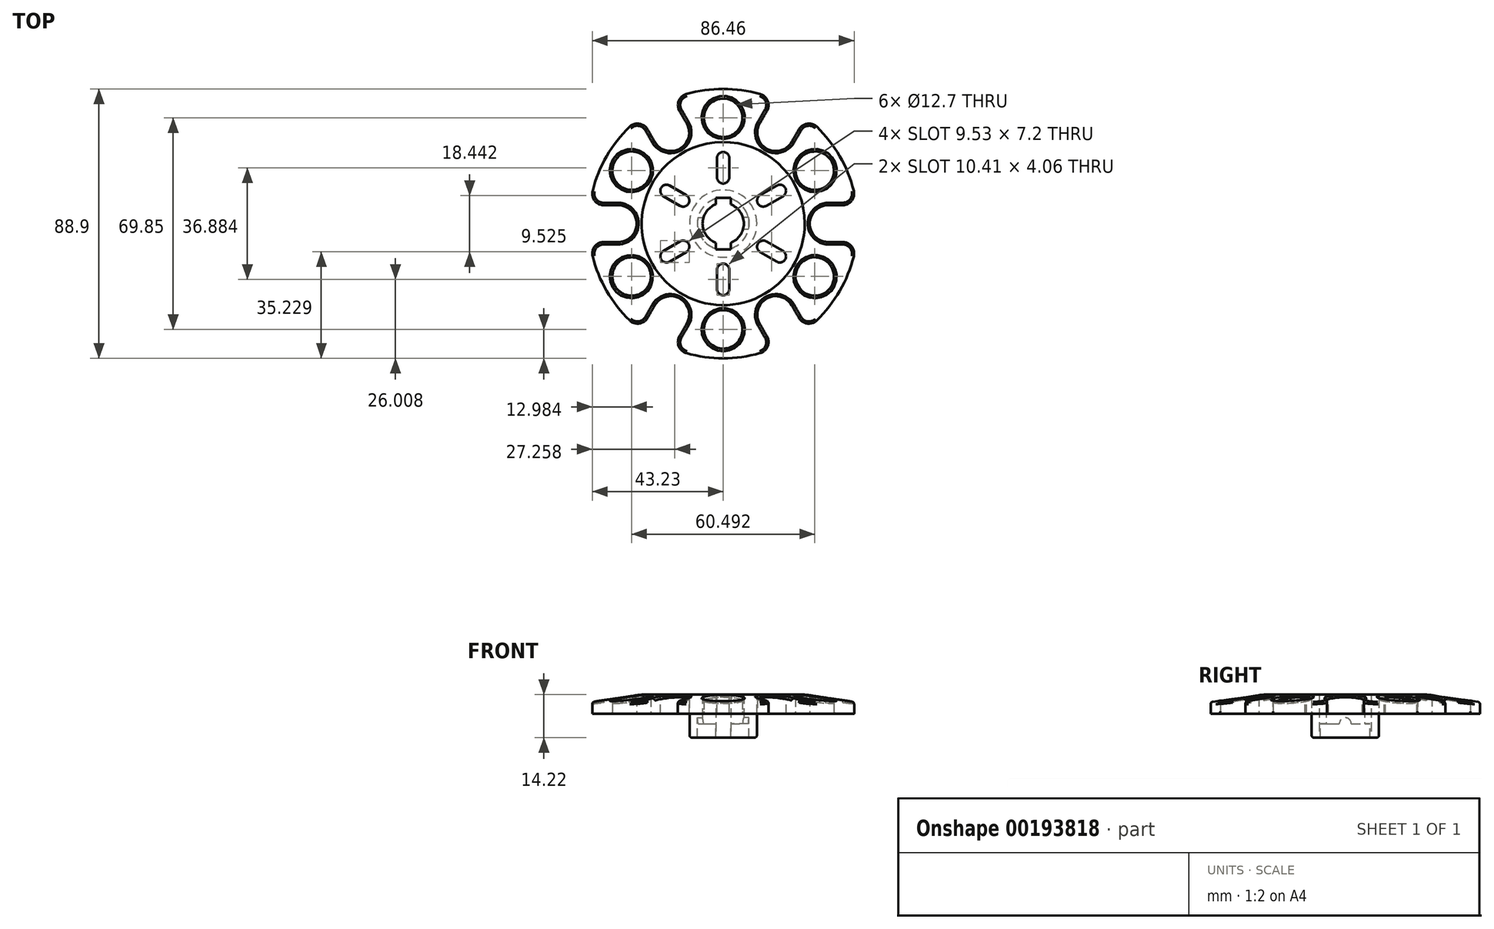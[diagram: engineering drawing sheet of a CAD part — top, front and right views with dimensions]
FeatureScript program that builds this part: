
annotation { "Feature Type Name" : "Feature", "Feature Type Description" : "" }
export const myFeature = defineFeature(function(context is Context, id is Id, definition is map)
    precondition{}
    {
        {
            var Q0;
            Q0=qCreatedBy(makeId("Top.planeOp"),FACE);
            var sketch = newSketch(context, id + "F0", { "sketchPlane" : qUnion([Q0])});
            skCircle(sketch, "E0", {"center": v(0, 0) * mm, "radius": 44.45 * mm, "construction": true});
            skArc(sketch, "E1", {"start": v(-2.48, 6.35) * mm, "mid": v(-6.82, 0) * mm, "end": v(-2.48, -6.35) * mm});
            skCircle(sketch, "E2", {"center": v(0, 0) * mm, "radius": 8.55 * mm, "construction": true});
            skLineSegment(sketch, "E3", {"start": v(0, 0) * mm, "end": v(0, 49.33) * mm, "construction": true});
            skLineSegment(sketch, "E4", {"start": v(-14.44, 42.04) * mm, "end": v(-14.44, 0) * mm, "construction": true});
            skArc(sketch, "E5", {"start": v(0, 44.45) * mm, "mid": v(-6.16, 44.02) * mm, "end": v(-12.2, 42.74) * mm});
            skLineSegment(sketch, "E6", {"start": v(0, 0) * mm, "end": v(-4.27, 7.4) * mm, "construction": true});
            skLineSegment(sketch, "E7", {"start": v(-14.44, 37.2) * mm, "end": v(-12.06, 33.07) * mm});
            skArc(sketch, "E8", {"start": v(-14.44, 37.2) * mm, "mid": v(-14.67, 40.52) * mm, "end": v(-12.2, 42.74) * mm});
            skCircle(sketch, "E9", {"center": v(0, 0) * mm, "radius": 28.58 * mm, "construction": true});
            skLineSegment(sketch, "E10.trimOffspring", {"start": v(-14.29, 24.75) * mm, "end": v(-22.23, 38.5) * mm, "construction": true});
            skArc(sketch, "E11", {"start": v(-14.44, 24.66) * mm, "mid": v(-11.47, 28.36) * mm, "end": v(-12.06, 33.07) * mm});
            skPoint(sketch, "E11.second.point", {"position": v(-20.38, 35.3) * mm});
            skPoint(sketch, "E11.third.point", {"position": v(-12.06, 33.07) * mm});
            skArc(sketch, "E12.MirrorCS", {"start": v(0, 44.45) * mm, "mid": v(6.16, 44.02) * mm, "end": v(12.2, 42.74) * mm});
            skArc(sketch, "E13.MirrorCS", {"start": v(14.44, 37.2) * mm, "mid": v(14.67, 40.52) * mm, "end": v(12.2, 42.74) * mm});
            skLineSegment(sketch, "E14.MirrorCS", {"start": v(14.44, 37.2) * mm, "end": v(12.06, 33.07) * mm});
            skArc(sketch, "E15.MirrorCS", {"start": v(14.44, 24.66) * mm, "mid": v(11.47, 28.36) * mm, "end": v(12.06, 33.07) * mm});
            skCircle(sketch, "E16", {"center": v(0, 34.93) * mm, "radius": 6.35 * mm});
            skLineSegment(sketch, "E17.anchor1", {"start": v(0, 0) * mm, "end": v(-14.44, 24.66) * mm, "construction": true});
            skLineSegment(sketch, "E17.anchor2", {"start": v(0, 0) * mm, "end": v(-14.44, 24.66) * mm, "construction": true});
            skArc(sketch, "E18.1.0", {"start": v(-28.58, -0.17) * mm, "mid": v(-30.3, 4.25) * mm, "end": v(-34.67, 6.1) * mm});
            skLineSegment(sketch, "E18.1.1", {"start": v(-39.44, 6.1) * mm, "end": v(-34.67, 6.1) * mm});
            skArc(sketch, "E18.1.2", {"start": v(-39.44, 6.1) * mm, "mid": v(-42.43, 7.56) * mm, "end": v(-43.12, 10.8) * mm});
            skCircle(sketch, "E18.1.3", {"center": v(-30.25, 17.46) * mm, "radius": 6.35 * mm});
            skArc(sketch, "E18.1.4", {"start": v(-25, 31.1) * mm, "mid": v(-27.76, 32.97) * mm, "end": v(-30.92, 31.93) * mm});
            skLineSegment(sketch, "E18.1.5", {"start": v(-25, 31.1) * mm, "end": v(-22.61, 26.98) * mm});
            skArc(sketch, "E18.1.6", {"start": v(-14.14, 24.84) * mm, "mid": v(-18.83, 24.12) * mm, "end": v(-22.61, 26.98) * mm});
            skArc(sketch, "E18.1.7", {"start": v(-38.5, 22.22) * mm, "mid": v(-35.04, 27.34) * mm, "end": v(-30.92, 31.93) * mm});
            skArc(sketch, "E18.1.8", {"start": v(-38.5, 22.23) * mm, "mid": v(-35.04, 27.34) * mm, "end": v(-30.92, 31.93) * mm});
            skArc(sketch, "E18.1.9", {"start": v(-38.5, 22.23) * mm, "mid": v(-35.04, 27.34) * mm, "end": v(-30.92, 31.93) * mm});
            skArc(sketch, "E18.1.10", {"start": v(-38.5, 22.23) * mm, "mid": v(-35.04, 27.34) * mm, "end": v(-30.92, 31.93) * mm});
            skArc(sketch, "E18.1.11", {"start": v(-38.5, 22.23) * mm, "mid": v(-35.04, 27.34) * mm, "end": v(-30.92, 31.93) * mm});
            skArc(sketch, "E18.1.12", {"start": v(-38.5, 22.23) * mm, "mid": v(-35.04, 27.34) * mm, "end": v(-30.92, 31.93) * mm});
            skArc(sketch, "E18.1.13", {"start": v(-38.5, 22.23) * mm, "mid": v(-41.2, 16.68) * mm, "end": v(-43.12, 10.8) * mm});
            skArc(sketch, "E18.1.14", {"start": v(-38.5, 22.23) * mm, "mid": v(-41.2, 16.68) * mm, "end": v(-43.12, 10.8) * mm});
            skArc(sketch, "E18.1.15", {"start": v(-38.5, 22.22) * mm, "mid": v(-41.2, 16.68) * mm, "end": v(-43.12, 10.8) * mm});
            skArc(sketch, "E18.1.16", {"start": v(-38.5, 22.23) * mm, "mid": v(-41.2, 16.68) * mm, "end": v(-43.12, 10.8) * mm});
            skArc(sketch, "E18.1.17", {"start": v(-38.5, 22.23) * mm, "mid": v(-41.2, 16.68) * mm, "end": v(-43.12, 10.8) * mm});
            skArc(sketch, "E18.1.18", {"start": v(-38.5, 22.23) * mm, "mid": v(-41.2, 16.68) * mm, "end": v(-43.12, 10.8) * mm});
            skArc(sketch, "E18.2.0", {"start": v(-14.14, -24.84) * mm, "mid": v(-18.83, -24.12) * mm, "end": v(-22.61, -26.98) * mm});
            skLineSegment(sketch, "E18.2.1", {"start": v(-25, -31.1) * mm, "end": v(-22.61, -26.98) * mm});
            skArc(sketch, "E18.2.2", {"start": v(-25, -31.1) * mm, "mid": v(-27.76, -32.97) * mm, "end": v(-30.92, -31.93) * mm});
            skCircle(sketch, "E18.2.3", {"center": v(-30.25, -17.46) * mm, "radius": 6.35 * mm});
            skArc(sketch, "E18.2.4", {"start": v(-39.44, -6.1) * mm, "mid": v(-42.43, -7.56) * mm, "end": v(-43.12, -10.8) * mm});
            skLineSegment(sketch, "E18.2.5", {"start": v(-39.44, -6.1) * mm, "end": v(-34.67, -6.1) * mm});
            skArc(sketch, "E18.2.6", {"start": v(-28.58, 0.17) * mm, "mid": v(-30.3, -4.25) * mm, "end": v(-34.67, -6.1) * mm});
            skArc(sketch, "E18.2.7", {"start": v(-38.5, -22.23) * mm, "mid": v(-41.2, -16.68) * mm, "end": v(-43.12, -10.8) * mm});
            skArc(sketch, "E18.2.8", {"start": v(-38.5, -22.22) * mm, "mid": v(-41.2, -16.68) * mm, "end": v(-43.12, -10.8) * mm});
            skArc(sketch, "E18.2.9", {"start": v(-38.5, -22.22) * mm, "mid": v(-41.2, -16.68) * mm, "end": v(-43.12, -10.8) * mm});
            skArc(sketch, "E18.2.10", {"start": v(-38.5, -22.22) * mm, "mid": v(-41.2, -16.68) * mm, "end": v(-43.12, -10.8) * mm});
            skArc(sketch, "E18.2.11", {"start": v(-38.5, -22.22) * mm, "mid": v(-41.2, -16.68) * mm, "end": v(-43.12, -10.8) * mm});
            skArc(sketch, "E18.2.12", {"start": v(-38.5, -22.22) * mm, "mid": v(-41.2, -16.68) * mm, "end": v(-43.12, -10.8) * mm});
            skArc(sketch, "E18.2.13", {"start": v(-38.5, -22.22) * mm, "mid": v(-35.04, -27.34) * mm, "end": v(-30.92, -31.93) * mm});
            skArc(sketch, "E18.2.14", {"start": v(-38.5, -22.22) * mm, "mid": v(-35.04, -27.34) * mm, "end": v(-30.92, -31.93) * mm});
            skArc(sketch, "E18.2.15", {"start": v(-38.5, -22.23) * mm, "mid": v(-35.04, -27.34) * mm, "end": v(-30.92, -31.93) * mm});
            skArc(sketch, "E18.2.16", {"start": v(-38.5, -22.23) * mm, "mid": v(-35.04, -27.34) * mm, "end": v(-30.92, -31.93) * mm});
            skArc(sketch, "E18.2.17", {"start": v(-38.5, -22.22) * mm, "mid": v(-35.04, -27.34) * mm, "end": v(-30.92, -31.93) * mm});
            skArc(sketch, "E18.2.18", {"start": v(-38.5, -22.22) * mm, "mid": v(-35.04, -27.34) * mm, "end": v(-30.92, -31.93) * mm});
            skArc(sketch, "E18.3.0", {"start": v(14.44, -24.66) * mm, "mid": v(11.47, -28.36) * mm, "end": v(12.06, -33.07) * mm});
            skLineSegment(sketch, "E18.3.1", {"start": v(14.44, -37.2) * mm, "end": v(12.06, -33.07) * mm});
            skArc(sketch, "E18.3.2", {"start": v(14.44, -37.2) * mm, "mid": v(14.67, -40.52) * mm, "end": v(12.2, -42.74) * mm});
            skCircle(sketch, "E18.3.3", {"center": v(0, -34.93) * mm, "radius": 6.35 * mm});
            skArc(sketch, "E18.3.4", {"start": v(-14.44, -37.2) * mm, "mid": v(-14.67, -40.52) * mm, "end": v(-12.2, -42.74) * mm});
            skLineSegment(sketch, "E18.3.5", {"start": v(-14.44, -37.2) * mm, "end": v(-12.06, -33.07) * mm});
            skArc(sketch, "E18.3.6", {"start": v(-14.44, -24.66) * mm, "mid": v(-11.47, -28.36) * mm, "end": v(-12.06, -33.07) * mm});
            skArc(sketch, "E18.3.7", {"start": v(0, -44.45) * mm, "mid": v(-6.16, -44.02) * mm, "end": v(-12.2, -42.74) * mm});
            skArc(sketch, "E18.3.8", {"start": v(0, -44.45) * mm, "mid": v(-6.16, -44.02) * mm, "end": v(-12.2, -42.74) * mm});
            skArc(sketch, "E18.3.9", {"start": v(0, -44.45) * mm, "mid": v(-6.16, -44.02) * mm, "end": v(-12.2, -42.74) * mm});
            skArc(sketch, "E18.3.10", {"start": v(0, -44.45) * mm, "mid": v(-6.16, -44.02) * mm, "end": v(-12.2, -42.74) * mm});
            skArc(sketch, "E18.3.11", {"start": v(0, -44.45) * mm, "mid": v(-6.16, -44.02) * mm, "end": v(-12.2, -42.74) * mm});
            skArc(sketch, "E18.3.12", {"start": v(0, -44.45) * mm, "mid": v(-6.16, -44.02) * mm, "end": v(-12.2, -42.74) * mm});
            skArc(sketch, "E18.3.13", {"start": v(0, -44.45) * mm, "mid": v(6.16, -44.02) * mm, "end": v(12.2, -42.74) * mm});
            skArc(sketch, "E18.3.14", {"start": v(0, -44.45) * mm, "mid": v(6.16, -44.02) * mm, "end": v(12.2, -42.74) * mm});
            skArc(sketch, "E18.3.15", {"start": v(0, -44.45) * mm, "mid": v(6.16, -44.02) * mm, "end": v(12.2, -42.74) * mm});
            skArc(sketch, "E18.3.16", {"start": v(0, -44.45) * mm, "mid": v(6.16, -44.02) * mm, "end": v(12.2, -42.74) * mm});
            skArc(sketch, "E18.3.17", {"start": v(0, -44.45) * mm, "mid": v(6.16, -44.02) * mm, "end": v(12.2, -42.74) * mm});
            skArc(sketch, "E18.3.18", {"start": v(0, -44.45) * mm, "mid": v(6.16, -44.02) * mm, "end": v(12.2, -42.74) * mm});
            skArc(sketch, "E18.4.0", {"start": v(28.58, 0.17) * mm, "mid": v(30.3, -4.25) * mm, "end": v(34.67, -6.1) * mm});
            skLineSegment(sketch, "E18.4.1", {"start": v(39.44, -6.1) * mm, "end": v(34.67, -6.1) * mm});
            skArc(sketch, "E18.4.2", {"start": v(39.44, -6.1) * mm, "mid": v(42.43, -7.56) * mm, "end": v(43.12, -10.8) * mm});
            skCircle(sketch, "E18.4.3", {"center": v(30.25, -17.46) * mm, "radius": 6.35 * mm});
            skArc(sketch, "E18.4.4", {"start": v(25, -31.1) * mm, "mid": v(27.76, -32.97) * mm, "end": v(30.92, -31.93) * mm});
            skLineSegment(sketch, "E18.4.5", {"start": v(25, -31.1) * mm, "end": v(22.61, -26.98) * mm});
            skArc(sketch, "E18.4.6", {"start": v(14.14, -24.84) * mm, "mid": v(18.83, -24.12) * mm, "end": v(22.61, -26.98) * mm});
            skArc(sketch, "E18.4.7", {"start": v(38.5, -22.23) * mm, "mid": v(35.04, -27.34) * mm, "end": v(30.92, -31.93) * mm});
            skArc(sketch, "E18.4.8", {"start": v(38.5, -22.23) * mm, "mid": v(35.04, -27.34) * mm, "end": v(30.92, -31.93) * mm});
            skArc(sketch, "E18.4.9", {"start": v(38.5, -22.23) * mm, "mid": v(35.04, -27.34) * mm, "end": v(30.92, -31.93) * mm});
            skArc(sketch, "E18.4.10", {"start": v(38.5, -22.23) * mm, "mid": v(35.04, -27.34) * mm, "end": v(30.92, -31.93) * mm});
            skArc(sketch, "E18.4.11", {"start": v(38.5, -22.23) * mm, "mid": v(35.04, -27.34) * mm, "end": v(30.92, -31.93) * mm});
            skArc(sketch, "E18.4.12", {"start": v(38.5, -22.23) * mm, "mid": v(35.04, -27.34) * mm, "end": v(30.92, -31.93) * mm});
            skArc(sketch, "E18.4.13", {"start": v(38.5, -22.23) * mm, "mid": v(41.2, -16.68) * mm, "end": v(43.12, -10.8) * mm});
            skArc(sketch, "E18.4.14", {"start": v(38.5, -22.23) * mm, "mid": v(41.2, -16.68) * mm, "end": v(43.12, -10.8) * mm});
            skArc(sketch, "E18.4.15", {"start": v(38.5, -22.23) * mm, "mid": v(41.2, -16.68) * mm, "end": v(43.12, -10.8) * mm});
            skArc(sketch, "E18.4.16", {"start": v(38.5, -22.23) * mm, "mid": v(41.2, -16.68) * mm, "end": v(43.12, -10.8) * mm});
            skArc(sketch, "E18.4.17", {"start": v(38.5, -22.23) * mm, "mid": v(41.2, -16.68) * mm, "end": v(43.12, -10.8) * mm});
            skArc(sketch, "E18.4.18", {"start": v(38.5, -22.23) * mm, "mid": v(41.2, -16.68) * mm, "end": v(43.12, -10.8) * mm});
            skArc(sketch, "E18.5.0", {"start": v(14.14, 24.84) * mm, "mid": v(18.83, 24.12) * mm, "end": v(22.61, 26.98) * mm});
            skLineSegment(sketch, "E18.5.1", {"start": v(25, 31.1) * mm, "end": v(22.61, 26.98) * mm});
            skArc(sketch, "E18.5.2", {"start": v(25, 31.1) * mm, "mid": v(27.76, 32.97) * mm, "end": v(30.92, 31.93) * mm});
            skCircle(sketch, "E18.5.3", {"center": v(30.25, 17.46) * mm, "radius": 6.35 * mm});
            skArc(sketch, "E18.5.4", {"start": v(39.44, 6.1) * mm, "mid": v(42.43, 7.56) * mm, "end": v(43.12, 10.8) * mm});
            skLineSegment(sketch, "E18.5.5", {"start": v(39.44, 6.1) * mm, "end": v(34.67, 6.1) * mm});
            skArc(sketch, "E18.5.6", {"start": v(28.58, -0.17) * mm, "mid": v(30.3, 4.25) * mm, "end": v(34.67, 6.1) * mm});
            skArc(sketch, "E18.5.7", {"start": v(38.5, 22.23) * mm, "mid": v(41.2, 16.68) * mm, "end": v(43.12, 10.8) * mm});
            skArc(sketch, "E18.5.8", {"start": v(38.5, 22.23) * mm, "mid": v(41.2, 16.68) * mm, "end": v(43.12, 10.8) * mm});
            skArc(sketch, "E18.5.9", {"start": v(38.5, 22.23) * mm, "mid": v(41.2, 16.68) * mm, "end": v(43.12, 10.8) * mm});
            skArc(sketch, "E18.5.10", {"start": v(38.5, 22.22) * mm, "mid": v(41.2, 16.68) * mm, "end": v(43.12, 10.8) * mm});
            skArc(sketch, "E18.5.11", {"start": v(38.5, 22.23) * mm, "mid": v(41.2, 16.68) * mm, "end": v(43.12, 10.8) * mm});
            skArc(sketch, "E18.5.12", {"start": v(38.5, 22.23) * mm, "mid": v(41.2, 16.68) * mm, "end": v(43.12, 10.8) * mm});
            skArc(sketch, "E18.5.13", {"start": v(38.5, 22.23) * mm, "mid": v(35.04, 27.34) * mm, "end": v(30.92, 31.93) * mm});
            skArc(sketch, "E18.5.14", {"start": v(38.5, 22.23) * mm, "mid": v(35.04, 27.34) * mm, "end": v(30.92, 31.93) * mm});
            skArc(sketch, "E18.5.15", {"start": v(38.5, 22.23) * mm, "mid": v(35.04, 27.34) * mm, "end": v(30.92, 31.93) * mm});
            skArc(sketch, "E18.5.16", {"start": v(38.5, 22.23) * mm, "mid": v(35.04, 27.34) * mm, "end": v(30.92, 31.93) * mm});
            skArc(sketch, "E18.5.17", {"start": v(38.5, 22.23) * mm, "mid": v(35.04, 27.34) * mm, "end": v(30.92, 31.93) * mm});
            skArc(sketch, "E18.5.18", {"start": v(38.5, 22.23) * mm, "mid": v(35.04, 27.34) * mm, "end": v(30.92, 31.93) * mm});
            skLineSegment(sketch, "E19.bottom", {"start": v(2.48, 8.55) * mm, "end": v(-2.48, 8.55) * mm});
            skLineSegment(sketch, "E19.top", {"start": v(2.48, -8.55) * mm, "end": v(-2.48, -8.55) * mm});
            skLineSegment(sketch, "E19.left", {"start": v(2.48, 8.55) * mm, "end": v(2.48, -8.55) * mm});
            skLineSegment(sketch, "E19.right", {"start": v(-2.48, 8.55) * mm, "end": v(-2.48, -8.55) * mm});
            skArc(sketch, "E20.trimOffspring", {"start": v(2.48, -6.35) * mm, "mid": v(6.82, 0) * mm, "end": v(2.48, 6.35) * mm});
            skSolve(sketch);
        }
        {
            var Q0;
            Q0=makeQuery(id+"F0.imprint","IMPRINT",FACE,{"disambiguationData":[TD([[makeQuery(id+"F0.imprint","IMPRINT",EDGE,{"derivedFrom":sQuery(id+"F0.wireOp",EDGE,"E1")}),-1.0]])]});
            extrude(context, id + "F1", {"entities" : qUnion([Q0]), "depth" : 6.35 * mm});
        }
        {
            var Q0;
            Q0=makeQuery(id+"F1.opExtrude","CAP_FACE",FACE,{"disambiguationData":[OSD([sQuery(id+"F0.wireOp",EDGE,"E1"),sQuery(id+"F0.wireOp",EDGE,"E11"),sQuery(id+"F0.wireOp",EDGE,"E7"),sQuery(id+"F0.wireOp",EDGE,"E8"),sQuery(id+"F0.wireOp",EDGE,"E5"),sQuery(id+"F0.wireOp",EDGE,"E12.MirrorCS"),sQuery(id+"F0.wireOp",EDGE,"E13.MirrorCS"),sQuery(id+"F0.wireOp",EDGE,"E14.MirrorCS"),sQuery(id+"F0.wireOp",EDGE,"E15.MirrorCS"),sQuery(id+"F0.wireOp",EDGE,"E16"),sQuery(id+"F0.wireOp",EDGE,"E18.1.0"),sQuery(id+"F0.wireOp",EDGE,"E18.1.1"),sQuery(id+"F0.wireOp",EDGE,"E18.1.2"),sQuery(id+"F0.wireOp",EDGE,"E18.1.3"),sQuery(id+"F0.wireOp",EDGE,"E18.1.4"),sQuery(id+"F0.wireOp",EDGE,"E18.1.5"),sQuery(id+"F0.wireOp",EDGE,"E18.1.6"),sQuery(id+"F0.wireOp",EDGE,"E18.1.12"),sQuery(id+"F0.wireOp",EDGE,"E18.1.18"),sQuery(id+"F0.wireOp",EDGE,"E18.2.0"),sQuery(id+"F0.wireOp",EDGE,"E18.2.1"),sQuery(id+"F0.wireOp",EDGE,"E18.2.2"),sQuery(id+"F0.wireOp",EDGE,"E18.2.3"),sQuery(id+"F0.wireOp",EDGE,"E18.2.4"),sQuery(id+"F0.wireOp",EDGE,"E18.2.5"),sQuery(id+"F0.wireOp",EDGE,"E18.2.6"),sQuery(id+"F0.wireOp",EDGE,"E18.2.12"),sQuery(id+"F0.wireOp",EDGE,"E18.2.18"),sQuery(id+"F0.wireOp",EDGE,"E18.3.0"),sQuery(id+"F0.wireOp",EDGE,"E18.3.1"),sQuery(id+"F0.wireOp",EDGE,"E18.3.2"),sQuery(id+"F0.wireOp",EDGE,"E18.3.3"),sQuery(id+"F0.wireOp",EDGE,"E18.3.4"),sQuery(id+"F0.wireOp",EDGE,"E18.3.5"),sQuery(id+"F0.wireOp",EDGE,"E18.3.6"),sQuery(id+"F0.wireOp",EDGE,"E18.3.12"),sQuery(id+"F0.wireOp",EDGE,"E18.3.18"),sQuery(id+"F0.wireOp",EDGE,"E18.4.0"),sQuery(id+"F0.wireOp",EDGE,"E18.4.1"),sQuery(id+"F0.wireOp",EDGE,"E18.4.2"),sQuery(id+"F0.wireOp",EDGE,"E18.4.3"),sQuery(id+"F0.wireOp",EDGE,"E18.4.4"),sQuery(id+"F0.wireOp",EDGE,"E18.4.5"),sQuery(id+"F0.wireOp",EDGE,"E18.4.6"),sQuery(id+"F0.wireOp",EDGE,"E18.4.12"),sQuery(id+"F0.wireOp",EDGE,"E18.4.18"),sQuery(id+"F0.wireOp",EDGE,"E18.5.0"),sQuery(id+"F0.wireOp",EDGE,"E18.5.1"),sQuery(id+"F0.wireOp",EDGE,"E18.5.2"),sQuery(id+"F0.wireOp",EDGE,"E18.5.3"),sQuery(id+"F0.wireOp",EDGE,"E18.5.4"),sQuery(id+"F0.wireOp",EDGE,"E18.5.5"),sQuery(id+"F0.wireOp",EDGE,"E18.5.6"),sQuery(id+"F0.wireOp",EDGE,"E18.5.12"),sQuery(id+"F0.wireOp",EDGE,"E18.5.18"),sQuery(id+"F0.wireOp",EDGE,"E19.bottom"),sQuery(id+"F0.wireOp",EDGE,"E19.top"),sQuery(id+"F0.wireOp",EDGE,"E19.left"),sQuery(id+"F0.wireOp",EDGE,"E19.right"),sQuery(id+"F0.wireOp",EDGE,"E20.trimOffspring")])],"isStart":false});
            var sketch = newSketch(context, id + "F2", { "sketchPlane" : qUnion([Q0])});
            skCircle(sketch, "E21", {"center": v(0, 0) * mm, "radius": 8.55 * mm});
            skCircle(sketch, "E22", {"center": v(0, 0) * mm, "radius": 11.11 * mm});
            skSolve(sketch);
        }
        {
            var Q0;
            Q0=makeQuery(id+"F2.imprint","IMPRINT",FACE,{"disambiguationData":[TD([[makeQuery(id+"F2.imprint","IMPRINT",EDGE,{"derivedFrom":sQuery(id+"F2.wireOp",EDGE,"E22")}),1.0]])]});
            extrude(context, id + "F3", {"entities" : qUnion([Q0]), "operationType" : NewBodyOperationType.ADD, "oppositeDirection" : true, "depth" : 14.22 * mm});
        }
        {
            var Q0;
            Q0=makeQuery(id+"F1.opExtrude","CAP_FACE",FACE,{"disambiguationData":[OSD([sQuery(id+"F0.wireOp",EDGE,"E1"),sQuery(id+"F0.wireOp",EDGE,"E11"),sQuery(id+"F0.wireOp",EDGE,"E7"),sQuery(id+"F0.wireOp",EDGE,"E8"),sQuery(id+"F0.wireOp",EDGE,"E5"),sQuery(id+"F0.wireOp",EDGE,"E12.MirrorCS"),sQuery(id+"F0.wireOp",EDGE,"E13.MirrorCS"),sQuery(id+"F0.wireOp",EDGE,"E14.MirrorCS"),sQuery(id+"F0.wireOp",EDGE,"E15.MirrorCS"),sQuery(id+"F0.wireOp",EDGE,"E16"),sQuery(id+"F0.wireOp",EDGE,"E18.1.0"),sQuery(id+"F0.wireOp",EDGE,"E18.1.1"),sQuery(id+"F0.wireOp",EDGE,"E18.1.2"),sQuery(id+"F0.wireOp",EDGE,"E18.1.3"),sQuery(id+"F0.wireOp",EDGE,"E18.1.4"),sQuery(id+"F0.wireOp",EDGE,"E18.1.5"),sQuery(id+"F0.wireOp",EDGE,"E18.1.6"),sQuery(id+"F0.wireOp",EDGE,"E18.1.12"),sQuery(id+"F0.wireOp",EDGE,"E18.1.18"),sQuery(id+"F0.wireOp",EDGE,"E18.2.0"),sQuery(id+"F0.wireOp",EDGE,"E18.2.1"),sQuery(id+"F0.wireOp",EDGE,"E18.2.2"),sQuery(id+"F0.wireOp",EDGE,"E18.2.3"),sQuery(id+"F0.wireOp",EDGE,"E18.2.4"),sQuery(id+"F0.wireOp",EDGE,"E18.2.5"),sQuery(id+"F0.wireOp",EDGE,"E18.2.6"),sQuery(id+"F0.wireOp",EDGE,"E18.2.12"),sQuery(id+"F0.wireOp",EDGE,"E18.2.18"),sQuery(id+"F0.wireOp",EDGE,"E18.3.0"),sQuery(id+"F0.wireOp",EDGE,"E18.3.1"),sQuery(id+"F0.wireOp",EDGE,"E18.3.2"),sQuery(id+"F0.wireOp",EDGE,"E18.3.3"),sQuery(id+"F0.wireOp",EDGE,"E18.3.4"),sQuery(id+"F0.wireOp",EDGE,"E18.3.5"),sQuery(id+"F0.wireOp",EDGE,"E18.3.6"),sQuery(id+"F0.wireOp",EDGE,"E18.3.12"),sQuery(id+"F0.wireOp",EDGE,"E18.3.18"),sQuery(id+"F0.wireOp",EDGE,"E18.4.0"),sQuery(id+"F0.wireOp",EDGE,"E18.4.1"),sQuery(id+"F0.wireOp",EDGE,"E18.4.2"),sQuery(id+"F0.wireOp",EDGE,"E18.4.3"),sQuery(id+"F0.wireOp",EDGE,"E18.4.4"),sQuery(id+"F0.wireOp",EDGE,"E18.4.5"),sQuery(id+"F0.wireOp",EDGE,"E18.4.6"),sQuery(id+"F0.wireOp",EDGE,"E18.4.12"),sQuery(id+"F0.wireOp",EDGE,"E18.4.18"),sQuery(id+"F0.wireOp",EDGE,"E18.5.0"),sQuery(id+"F0.wireOp",EDGE,"E18.5.1"),sQuery(id+"F0.wireOp",EDGE,"E18.5.2"),sQuery(id+"F0.wireOp",EDGE,"E18.5.3"),sQuery(id+"F0.wireOp",EDGE,"E18.5.4"),sQuery(id+"F0.wireOp",EDGE,"E18.5.5"),sQuery(id+"F0.wireOp",EDGE,"E18.5.6"),sQuery(id+"F0.wireOp",EDGE,"E18.5.12"),sQuery(id+"F0.wireOp",EDGE,"E18.5.18"),sQuery(id+"F0.wireOp",EDGE,"E19.bottom"),sQuery(id+"F0.wireOp",EDGE,"E19.top"),sQuery(id+"F0.wireOp",EDGE,"E19.left"),sQuery(id+"F0.wireOp",EDGE,"E19.right"),sQuery(id+"F0.wireOp",EDGE,"E20.trimOffspring")])],"isStart":false});
            var sketch = newSketch(context, id + "F4", { "sketchPlane" : qUnion([Q0])});
            skArc(sketch, "E23", {"start": v(-2.48, 6.35) * mm, "mid": v(-6.82, 0) * mm, "end": v(-2.48, -6.35) * mm});
            skArc(sketch, "E24", {"start": v(-2.48, 8.18) * mm, "mid": v(-8.55, 0) * mm, "end": v(-2.48, -8.18) * mm});
            skLineSegment(sketch, "E25", {"start": v(-2.48, 6.35) * mm, "end": v(-2.48, 8.55) * mm});
            skLineSegment(sketch, "E26", {"start": v(-2.48, 8.55) * mm, "end": v(2.48, 8.55) * mm});
            skLineSegment(sketch, "E27", {"start": v(2.48, 8.55) * mm, "end": v(2.48, 6.35) * mm});
            skLineSegment(sketch, "E28", {"start": v(-2.48, -6.35) * mm, "end": v(-2.48, -8.55) * mm});
            skLineSegment(sketch, "E29", {"start": v(-2.48, -8.55) * mm, "end": v(2.48, -8.55) * mm});
            skLineSegment(sketch, "E30", {"start": v(2.48, -8.55) * mm, "end": v(2.48, -6.35) * mm});
            skArc(sketch, "E31.trimOffspring", {"start": v(2.48, -6.35) * mm, "mid": v(6.82, 0) * mm, "end": v(2.48, 6.35) * mm});
            skArc(sketch, "E32.trimOffspring", {"start": v(2.48, -8.18) * mm, "mid": v(8.55, 0) * mm, "end": v(2.48, 8.18) * mm});
            skSolve(sketch);
        }
        {
            var Q0;
            {var subQ0=sQuery(id+"F4.wireOp",EDGE,"E31.trimOffspring");Q0=makeQuery(id+"F4.imprint","IMPRINT",FACE,{"disambiguationData":[TD([[makeQuery(id+"F4.imprint","IMPRINT",EDGE,{"derivedFrom":subQ0}),-1.0]])]});}
            var Q1;
            {var subQ0=sQuery(id+"F4.wireOp",EDGE,"E23");Q1=makeQuery(id+"F4.imprint","IMPRINT",FACE,{"disambiguationData":[TD([[makeQuery(id+"F4.imprint","IMPRINT",EDGE,{"derivedFrom":subQ0}),-1.0]])]});}
            extrude(context, id + "F5", {"entities" : qUnion([Q0, Q1]), "operationType" : NewBodyOperationType.ADD, "oppositeDirection" : true, "depth" : 9.65 * mm});
        }
        {
            var Q0;
            Q0=qCreatedBy(makeId("Right.planeOp"),FACE);
            var sketch = newSketch(context, id + "F6", { "sketchPlane" : qUnion([Q0])});
            skLineSegment(sketch, "E33", {"start": v(11.75, -3.3) * mm, "end": v(-12.2, -3.3) * mm, "construction": true});
            skLineSegment(sketch, "E34", {"start": v(0, 0) * mm, "end": v(0, -3.3) * mm, "construction": true});
            skCircle(sketch, "E35", {"center": v(0, -3.3) * mm, "radius": 1.97 * mm});
            skSolve(sketch);
        }
        {
            var Q0;
            Q0=makeQuery(id+"F6.imprint","IMPRINT",FACE,{"disambiguationData":[TD([[makeQuery(id+"F6.imprint","IMPRINT",EDGE,{"derivedFrom":sQuery(id+"F6.wireOp",EDGE,"E35")}),1.0]])]});
            var Q1;
            {var subQ0=sQuery(id+"F2.wireOp",EDGE,"E21");var subQ1=sQuery(id+"F0.wireOp",EDGE,"E19.right");var subQ2=sQuery(id+"F0.wireOp",EDGE,"E1");Q1=makeQuery(id+"F3.opExtrude","SWEPT_FACE",FACE,{"disambiguationData":[OSD([subQ0]),TDD([makeQuery(id+"F2.imprint","IMPRINT",EDGE,{"disambiguationData":[TD([[makeQuery(id+"F2.imprint","INTERSECT",VERTEX,{"derivedFrom":[makeQuery(id+"F1.opExtrude","CAP_EDGE",EDGE,{"disambiguationData":[OSD([subQ1]),TDD([makeQuery(id+"F0.imprint","IMPRINT",EDGE,{"disambiguationData":[TD([[makeQuery(id+"F0.imprint","INTERSECT",VERTEX,{"disambiguationData":[OD(0.0)],"derivedFrom":[subQ2,subQ1]}),1.0]])],"derivedFrom":subQ1})])],"isStart":false}),subQ0]}),-1.0]])],"derivedFrom":subQ0})])]});}
            extrude(context, id + "F7", {"entities" : qUnion([Q0]), "operationType" : NewBodyOperationType.REMOVE, "endBound" : BoundingType.UP_TO_SURFACE, "oppositeDirection" : true, "endBoundEntityFace" : qUnion([Q1]), "depth" : 25.4 * mm});
        }
        {
            var Q0;
            Q0=makeQuery(id+"F6.imprint","IMPRINT",FACE,{"disambiguationData":[TD([[makeQuery(id+"F6.imprint","IMPRINT",EDGE,{"derivedFrom":sQuery(id+"F6.wireOp",EDGE,"E35")}),1.0]])]});
            var Q1;
            {var subQ0=sQuery(id+"F2.wireOp",EDGE,"E21");var subQ1=sQuery(id+"F0.wireOp",EDGE,"E19.left");Q1=makeQuery(id+"F3.opExtrude","SWEPT_FACE",FACE,{"disambiguationData":[OSD([subQ0]),TDD([makeQuery(id+"F2.imprint","IMPRINT",EDGE,{"disambiguationData":[TD([[makeQuery(id+"F2.imprint","INTERSECT",VERTEX,{"derivedFrom":[makeQuery(id+"F1.opExtrude","CAP_EDGE",EDGE,{"disambiguationData":[OSD([subQ1]),TDD([makeQuery(id+"F0.imprint","IMPRINT",EDGE,{"disambiguationData":[TD([[makeQuery(id+"F0.imprint","INTERSECT",VERTEX,{"derivedFrom":[sQuery(id+"F0.wireOp",EDGE,"E19.bottom"),subQ1]}),-1.0]])],"derivedFrom":subQ1})])],"isStart":false}),subQ0]}),1.0]])],"derivedFrom":subQ0})])]});}
            extrude(context, id + "F8", {"entities" : qUnion([Q0]), "operationType" : NewBodyOperationType.REMOVE, "endBound" : BoundingType.UP_TO_SURFACE, "endBoundEntityFace" : qUnion([Q1]), "depth" : 25.4 * mm});
        }
        {
            var Q0;
            Q0=makeQuery(id+"F1.opExtrude","CAP_FACE",FACE,{"disambiguationData":[OSD([sQuery(id+"F0.wireOp",EDGE,"E1"),sQuery(id+"F0.wireOp",EDGE,"E11"),sQuery(id+"F0.wireOp",EDGE,"E7"),sQuery(id+"F0.wireOp",EDGE,"E8"),sQuery(id+"F0.wireOp",EDGE,"E5"),sQuery(id+"F0.wireOp",EDGE,"E12.MirrorCS"),sQuery(id+"F0.wireOp",EDGE,"E13.MirrorCS"),sQuery(id+"F0.wireOp",EDGE,"E14.MirrorCS"),sQuery(id+"F0.wireOp",EDGE,"E15.MirrorCS"),sQuery(id+"F0.wireOp",EDGE,"E16"),sQuery(id+"F0.wireOp",EDGE,"E18.1.0"),sQuery(id+"F0.wireOp",EDGE,"E18.1.1"),sQuery(id+"F0.wireOp",EDGE,"E18.1.2"),sQuery(id+"F0.wireOp",EDGE,"E18.1.3"),sQuery(id+"F0.wireOp",EDGE,"E18.1.4"),sQuery(id+"F0.wireOp",EDGE,"E18.1.5"),sQuery(id+"F0.wireOp",EDGE,"E18.1.6"),sQuery(id+"F0.wireOp",EDGE,"E18.1.12"),sQuery(id+"F0.wireOp",EDGE,"E18.1.18"),sQuery(id+"F0.wireOp",EDGE,"E18.2.0"),sQuery(id+"F0.wireOp",EDGE,"E18.2.1"),sQuery(id+"F0.wireOp",EDGE,"E18.2.2"),sQuery(id+"F0.wireOp",EDGE,"E18.2.3"),sQuery(id+"F0.wireOp",EDGE,"E18.2.4"),sQuery(id+"F0.wireOp",EDGE,"E18.2.5"),sQuery(id+"F0.wireOp",EDGE,"E18.2.6"),sQuery(id+"F0.wireOp",EDGE,"E18.2.12"),sQuery(id+"F0.wireOp",EDGE,"E18.2.18"),sQuery(id+"F0.wireOp",EDGE,"E18.3.0"),sQuery(id+"F0.wireOp",EDGE,"E18.3.1"),sQuery(id+"F0.wireOp",EDGE,"E18.3.2"),sQuery(id+"F0.wireOp",EDGE,"E18.3.3"),sQuery(id+"F0.wireOp",EDGE,"E18.3.4"),sQuery(id+"F0.wireOp",EDGE,"E18.3.5"),sQuery(id+"F0.wireOp",EDGE,"E18.3.6"),sQuery(id+"F0.wireOp",EDGE,"E18.3.12"),sQuery(id+"F0.wireOp",EDGE,"E18.3.18"),sQuery(id+"F0.wireOp",EDGE,"E18.4.0"),sQuery(id+"F0.wireOp",EDGE,"E18.4.1"),sQuery(id+"F0.wireOp",EDGE,"E18.4.2"),sQuery(id+"F0.wireOp",EDGE,"E18.4.3"),sQuery(id+"F0.wireOp",EDGE,"E18.4.4"),sQuery(id+"F0.wireOp",EDGE,"E18.4.5"),sQuery(id+"F0.wireOp",EDGE,"E18.4.6"),sQuery(id+"F0.wireOp",EDGE,"E18.4.12"),sQuery(id+"F0.wireOp",EDGE,"E18.4.18"),sQuery(id+"F0.wireOp",EDGE,"E18.5.0"),sQuery(id+"F0.wireOp",EDGE,"E18.5.1"),sQuery(id+"F0.wireOp",EDGE,"E18.5.2"),sQuery(id+"F0.wireOp",EDGE,"E18.5.3"),sQuery(id+"F0.wireOp",EDGE,"E18.5.4"),sQuery(id+"F0.wireOp",EDGE,"E18.5.5"),sQuery(id+"F0.wireOp",EDGE,"E18.5.6"),sQuery(id+"F0.wireOp",EDGE,"E18.5.12"),sQuery(id+"F0.wireOp",EDGE,"E18.5.18"),sQuery(id+"F0.wireOp",EDGE,"E19.bottom"),sQuery(id+"F0.wireOp",EDGE,"E19.top"),sQuery(id+"F0.wireOp",EDGE,"E19.left"),sQuery(id+"F0.wireOp",EDGE,"E19.right"),sQuery(id+"F0.wireOp",EDGE,"E20.trimOffspring")])],"isStart":false});
            var sketch = newSketch(context, id + "F9", { "sketchPlane" : qUnion([Q0])});
            skLineSegment(sketch, "E36.bottom", {"start": v(0, 23.65) * mm, "end": v(0, 23.65) * mm});
            skLineSegment(sketch, "E36.top", {"start": v(0, 13.24) * mm, "end": v(0, 13.24) * mm});
            skLineSegment(sketch, "E36.left", {"start": v(2.03, 21.62) * mm, "end": v(2.03, 15.27) * mm});
            skLineSegment(sketch, "E36.right", {"start": v(-2.03, 21.62) * mm, "end": v(-2.03, 15.27) * mm});
            skPoint(sketch, "E36.middle", {"position": v(0, 18.44) * mm});
            skArc(sketch, "E37", {"start": v(2.03, 21.62) * mm, "mid": v(0, 23.65) * mm, "end": v(-2.03, 21.62) * mm});
            skPoint(sketch, "E37.first.point", {"position": v(0, 23.65) * mm});
            skPoint(sketch, "E37.second.point", {"position": v(2.03, 21.62) * mm});
            skPoint(sketch, "E37.third.point", {"position": v(-2.03, 21.62) * mm});
            skArc(sketch, "E38", {"start": v(-2.03, 15.27) * mm, "mid": v(0, 13.24) * mm, "end": v(2.03, 15.27) * mm});
            skPoint(sketch, "E38.first.point", {"position": v(0, 13.24) * mm});
            skPoint(sketch, "E38.second.point", {"position": v(-2.03, 15.27) * mm});
            skPoint(sketch, "E38.third.point", {"position": v(2.03, 15.27) * mm});
            skLineSegment(sketch, "E39.1.0", {"start": v(-17.7, 12.57) * mm, "end": v(-12.2, 9.4) * mm});
            skPoint(sketch, "E39.1.1", {"position": v(-15.97, 9.22) * mm});
            skPoint(sketch, "E39.1.2", {"position": v(-14.24, 5.87) * mm});
            skArc(sketch, "E39.1.3", {"start": v(-14.24, 5.87) * mm, "mid": v(-11.46, 6.62) * mm, "end": v(-12.2, 9.4) * mm});
            skArc(sketch, "E39.1.4", {"start": v(-17.7, 12.57) * mm, "mid": v(-20.48, 11.82) * mm, "end": v(-19.74, 9.05) * mm});
            skLineSegment(sketch, "E39.1.5", {"start": v(-19.74, 9.05) * mm, "end": v(-14.24, 5.87) * mm});
            skPoint(sketch, "E39.1.6", {"position": v(-17.7, 12.57) * mm});
            skPoint(sketch, "E39.1.7", {"position": v(-12.2, 9.4) * mm});
            skPoint(sketch, "E39.1.8", {"position": v(-19.74, 9.05) * mm});
            skPoint(sketch, "E39.1.9", {"position": v(-11.46, 6.62) * mm});
            skPoint(sketch, "E39.1.10", {"position": v(-20.48, 11.82) * mm});
            skLineSegment(sketch, "E39.2.0", {"start": v(-19.74, -9.05) * mm, "end": v(-14.24, -5.87) * mm});
            skPoint(sketch, "E39.2.1", {"position": v(-15.97, -9.22) * mm});
            skPoint(sketch, "E39.2.2", {"position": v(-12.2, -9.4) * mm});
            skArc(sketch, "E39.2.3", {"start": v(-12.2, -9.4) * mm, "mid": v(-11.46, -6.62) * mm, "end": v(-14.24, -5.87) * mm});
            skArc(sketch, "E39.2.4", {"start": v(-19.74, -9.05) * mm, "mid": v(-20.48, -11.82) * mm, "end": v(-17.7, -12.57) * mm});
            skLineSegment(sketch, "E39.2.5", {"start": v(-17.7, -12.57) * mm, "end": v(-12.2, -9.4) * mm});
            skPoint(sketch, "E39.2.6", {"position": v(-19.74, -9.05) * mm});
            skPoint(sketch, "E39.2.7", {"position": v(-14.24, -5.87) * mm});
            skPoint(sketch, "E39.2.8", {"position": v(-17.7, -12.57) * mm});
            skPoint(sketch, "E39.2.9", {"position": v(-11.46, -6.62) * mm});
            skPoint(sketch, "E39.2.10", {"position": v(-20.48, -11.82) * mm});
            skLineSegment(sketch, "E39.3.0", {"start": v(-2.03, -21.62) * mm, "end": v(-2.03, -15.27) * mm});
            skPoint(sketch, "E39.3.1", {"position": v(0, -18.44) * mm});
            skPoint(sketch, "E39.3.2", {"position": v(2.03, -15.27) * mm});
            skArc(sketch, "E39.3.3", {"start": v(2.03, -15.27) * mm, "mid": v(0, -13.24) * mm, "end": v(-2.03, -15.27) * mm});
            skArc(sketch, "E39.3.4", {"start": v(-2.03, -21.62) * mm, "mid": v(0, -23.65) * mm, "end": v(2.03, -21.62) * mm});
            skLineSegment(sketch, "E39.3.5", {"start": v(2.03, -21.62) * mm, "end": v(2.03, -15.27) * mm});
            skPoint(sketch, "E39.3.6", {"position": v(-2.03, -21.62) * mm});
            skPoint(sketch, "E39.3.7", {"position": v(-2.03, -15.27) * mm});
            skPoint(sketch, "E39.3.8", {"position": v(2.03, -21.62) * mm});
            skPoint(sketch, "E39.3.9", {"position": v(0, -13.24) * mm});
            skPoint(sketch, "E39.3.10", {"position": v(0, -23.65) * mm});
            skLineSegment(sketch, "E39.4.0", {"start": v(17.7, -12.57) * mm, "end": v(12.2, -9.4) * mm});
            skPoint(sketch, "E39.4.1", {"position": v(15.97, -9.22) * mm});
            skPoint(sketch, "E39.4.2", {"position": v(14.24, -5.87) * mm});
            skArc(sketch, "E39.4.3", {"start": v(14.24, -5.87) * mm, "mid": v(11.46, -6.62) * mm, "end": v(12.2, -9.4) * mm});
            skArc(sketch, "E39.4.4", {"start": v(17.7, -12.57) * mm, "mid": v(20.48, -11.82) * mm, "end": v(19.74, -9.05) * mm});
            skLineSegment(sketch, "E39.4.5", {"start": v(19.74, -9.05) * mm, "end": v(14.24, -5.87) * mm});
            skPoint(sketch, "E39.4.6", {"position": v(17.7, -12.57) * mm});
            skPoint(sketch, "E39.4.7", {"position": v(12.2, -9.4) * mm});
            skPoint(sketch, "E39.4.8", {"position": v(19.74, -9.05) * mm});
            skPoint(sketch, "E39.4.9", {"position": v(11.46, -6.62) * mm});
            skPoint(sketch, "E39.4.10", {"position": v(20.48, -11.82) * mm});
            skLineSegment(sketch, "E39.5.0", {"start": v(19.74, 9.05) * mm, "end": v(14.24, 5.87) * mm});
            skPoint(sketch, "E39.5.1", {"position": v(15.97, 9.22) * mm});
            skPoint(sketch, "E39.5.2", {"position": v(12.2, 9.4) * mm});
            skArc(sketch, "E39.5.3", {"start": v(12.2, 9.4) * mm, "mid": v(11.46, 6.62) * mm, "end": v(14.24, 5.87) * mm});
            skArc(sketch, "E39.5.4", {"start": v(19.74, 9.05) * mm, "mid": v(20.48, 11.82) * mm, "end": v(17.7, 12.57) * mm});
            skLineSegment(sketch, "E39.5.5", {"start": v(17.7, 12.57) * mm, "end": v(12.2, 9.4) * mm});
            skPoint(sketch, "E39.5.6", {"position": v(19.74, 9.05) * mm});
            skPoint(sketch, "E39.5.7", {"position": v(14.24, 5.87) * mm});
            skPoint(sketch, "E39.5.8", {"position": v(17.7, 12.57) * mm});
            skPoint(sketch, "E39.5.9", {"position": v(11.46, 6.62) * mm});
            skPoint(sketch, "E39.5.10", {"position": v(20.48, 11.82) * mm});
            skPoint(sketch, "E39.center", {"position": v(0, 0) * mm});
            skSolve(sketch);
        }
        {
            var Q0;
            Q0=makeQuery(id+"F9.imprint","IMPRINT",FACE,{"disambiguationData":[TD([[makeQuery(id+"F9.imprint","IMPRINT",EDGE,{"derivedFrom":sQuery(id+"F9.wireOp",EDGE,"E36.left")}),-1.0]])]});
            var Q1;
            Q1=makeQuery(id+"F9.imprint","IMPRINT",FACE,{"disambiguationData":[TD([[makeQuery(id+"F9.imprint","IMPRINT",EDGE,{"derivedFrom":sQuery(id+"F9.wireOp",EDGE,"E39.5.0")}),-1.0]])]});
            var Q2;
            Q2=makeQuery(id+"F9.imprint","IMPRINT",FACE,{"disambiguationData":[TD([[makeQuery(id+"F9.imprint","IMPRINT",EDGE,{"derivedFrom":sQuery(id+"F9.wireOp",EDGE,"E39.4.0")}),-1.0]])]});
            var Q3;
            Q3=makeQuery(id+"F9.imprint","IMPRINT",FACE,{"disambiguationData":[TD([[makeQuery(id+"F9.imprint","IMPRINT",EDGE,{"derivedFrom":sQuery(id+"F9.wireOp",EDGE,"E39.3.0")}),-1.0]])]});
            var Q4;
            Q4=makeQuery(id+"F9.imprint","IMPRINT",FACE,{"disambiguationData":[TD([[makeQuery(id+"F9.imprint","IMPRINT",EDGE,{"derivedFrom":sQuery(id+"F9.wireOp",EDGE,"E39.2.0")}),-1.0]])]});
            var Q5;
            Q5=makeQuery(id+"F9.imprint","IMPRINT",FACE,{"disambiguationData":[TD([[makeQuery(id+"F9.imprint","IMPRINT",EDGE,{"derivedFrom":sQuery(id+"F9.wireOp",EDGE,"E39.1.0")}),-1.0]])]});
            extrude(context, id + "F10", {"entities" : qUnion([Q0, Q1, Q2, Q3, Q4, Q5]), "operationType" : NewBodyOperationType.REMOVE, "endBound" : BoundingType.THROUGH_ALL, "oppositeDirection" : true, "depth" : 25.4 * mm});
        }
        {
            var Q0;
            Q0=qCreatedBy(makeId("Right.planeOp"),FACE);
            var sketch = newSketch(context, id + "F11", { "sketchPlane" : qUnion([Q0])});
            skLineSegment(sketch, "E40", {"start": v(-44.7, 3.8) * mm, "end": v(-26.92, 6.35) * mm});
            skLineSegment(sketch, "E41", {"start": v(-26.92, 6.35) * mm, "end": v(-44.7, 6.35) * mm});
            skLineSegment(sketch, "E42", {"start": v(-44.7, 6.35) * mm, "end": v(-44.7, 3.8) * mm});
            skLineSegment(sketch, "E43", {"start": v(0, 0) * mm, "end": v(0, 11.33) * mm, "construction": true});
            skSolve(sketch);
        }
        {
            var Q0;
            Q0=makeQuery(id+"F11.imprint","IMPRINT",FACE,{"disambiguationData":[TD([[makeQuery(id+"F11.imprint","IMPRINT",EDGE,{"derivedFrom":sQuery(id+"F11.wireOp",EDGE,"E40")}),1.0]])]});
            var Q1;
            Q1=sQuery(id+"F11.wireOp",EDGE,"E43");
            revolve(context, id + "F12", {"operationType" : NewBodyOperationType.REMOVE, "entities" : qUnion([Q0]), "axis" : qUnion([Q1]), "revolveType" : RevolveType.FULL, "oppositeDirection" : true});
        }
        {
            var Q0;
            Q0=makeQuery(id+"F10.boolean.opBoolean","COPY",EDGE,{"derivedFrom":makeQuery(id+"F10.opExtrude","CAP_EDGE",EDGE,{"disambiguationData":[OSD([sQuery(id+"F9.wireOp",EDGE,"E39.5.5")])],"isStart":true})});
            var Q1;
            Q1=makeQuery(id+"F10.boolean.opBoolean","COPY",EDGE,{"derivedFrom":makeQuery(id+"F10.opExtrude","CAP_EDGE",EDGE,{"disambiguationData":[OSD([sQuery(id+"F9.wireOp",EDGE,"E36.right")])],"isStart":true})});
            var Q2;
            Q2=makeQuery(id+"F10.boolean.opBoolean","COPY",EDGE,{"derivedFrom":makeQuery(id+"F10.opExtrude","CAP_EDGE",EDGE,{"disambiguationData":[OSD([sQuery(id+"F9.wireOp",EDGE,"E39.1.0")])],"isStart":true})});
            var Q3;
            Q3=makeQuery(id+"F10.boolean.opBoolean","COPY",EDGE,{"derivedFrom":makeQuery(id+"F10.opExtrude","CAP_EDGE",EDGE,{"disambiguationData":[OSD([sQuery(id+"F9.wireOp",EDGE,"E39.2.0")])],"isStart":true})});
            var Q4;
            Q4=makeQuery(id+"F10.boolean.opBoolean","COPY",EDGE,{"derivedFrom":makeQuery(id+"F10.opExtrude","CAP_EDGE",EDGE,{"disambiguationData":[OSD([sQuery(id+"F9.wireOp",EDGE,"E39.3.0")])],"isStart":true})});
            var Q5;
            Q5=makeQuery(id+"F10.boolean.opBoolean","COPY",EDGE,{"derivedFrom":makeQuery(id+"F10.opExtrude","CAP_EDGE",EDGE,{"disambiguationData":[OSD([sQuery(id+"F9.wireOp",EDGE,"E39.4.5")])],"isStart":true})});
            var Q6;
            Q6=makeQuery(id+"F12.boolean.opBoolean","INTERSECT",EDGE,{"derivedFrom":[makeQuery(id+"F1.opExtrude","SWEPT_FACE",FACE,{"disambiguationData":[OSD([sQuery(id+"F0.wireOp",EDGE,"E18.2.0"),sQuery(id+"F0.wireOp",EDGE,"E18.3.6")])]}),makeQuery(id+"F12.opRevolve","SWEPT_FACE",FACE,{"disambiguationData":[OSD([sQuery(id+"F11.wireOp",EDGE,"E40")])]})]});
            var Q7;
            Q7=makeQuery(id+"F12.boolean.opBoolean","INTERSECT",EDGE,{"derivedFrom":[makeQuery(id+"F1.opExtrude","SWEPT_FACE",FACE,{"disambiguationData":[OSD([sQuery(id+"F0.wireOp",EDGE,"E18.2.3")])]}),makeQuery(id+"F12.opRevolve","SWEPT_FACE",FACE,{"disambiguationData":[OSD([sQuery(id+"F11.wireOp",EDGE,"E40")])]})]});
            var Q8;
            Q8=makeQuery(id+"F12.boolean.opBoolean","INTERSECT",EDGE,{"derivedFrom":[makeQuery(id+"F1.opExtrude","SWEPT_FACE",FACE,{"disambiguationData":[OSD([sQuery(id+"F0.wireOp",EDGE,"E18.1.3")])]}),makeQuery(id+"F12.opRevolve","SWEPT_FACE",FACE,{"disambiguationData":[OSD([sQuery(id+"F11.wireOp",EDGE,"E40")])]})]});
            var Q9;
            Q9=makeQuery(id+"F12.boolean.opBoolean","INTERSECT",EDGE,{"derivedFrom":[makeQuery(id+"F1.opExtrude","SWEPT_FACE",FACE,{"disambiguationData":[OSD([sQuery(id+"F0.wireOp",EDGE,"E16")])]}),makeQuery(id+"F12.opRevolve","SWEPT_FACE",FACE,{"disambiguationData":[OSD([sQuery(id+"F11.wireOp",EDGE,"E40")])]})]});
            var Q10;
            Q10=makeQuery(id+"F12.boolean.opBoolean","INTERSECT",EDGE,{"derivedFrom":[makeQuery(id+"F1.opExtrude","SWEPT_FACE",FACE,{"disambiguationData":[OSD([sQuery(id+"F0.wireOp",EDGE,"E18.5.3")])]}),makeQuery(id+"F12.opRevolve","SWEPT_FACE",FACE,{"disambiguationData":[OSD([sQuery(id+"F11.wireOp",EDGE,"E40")])]})]});
            var Q11;
            Q11=makeQuery(id+"F12.boolean.opBoolean","INTERSECT",EDGE,{"derivedFrom":[makeQuery(id+"F1.opExtrude","SWEPT_FACE",FACE,{"disambiguationData":[OSD([sQuery(id+"F0.wireOp",EDGE,"E18.4.3")])]}),makeQuery(id+"F12.opRevolve","SWEPT_FACE",FACE,{"disambiguationData":[OSD([sQuery(id+"F11.wireOp",EDGE,"E40")])]})]});
            var Q12;
            Q12=makeQuery(id+"F12.boolean.opBoolean","INTERSECT",EDGE,{"derivedFrom":[makeQuery(id+"F1.opExtrude","SWEPT_FACE",FACE,{"disambiguationData":[OSD([sQuery(id+"F0.wireOp",EDGE,"E18.3.3")])]}),makeQuery(id+"F12.opRevolve","SWEPT_FACE",FACE,{"disambiguationData":[OSD([sQuery(id+"F11.wireOp",EDGE,"E40")])]})]});
            fillet(context, id + "F13", {"entities" : qUnion([Q0, Q1, Q2, Q3, Q4, Q5, Q6, Q7, Q8, Q9, Q10, Q11, Q12]), "radius" : 0.76 * mm, "tangentPropagation" : true, "allowEdgeOverflow" : false});
        }
        {
            var Q0;
            Q0=makeQuery(id+"F3.opExtrude","CAP_EDGE",EDGE,{"disambiguationData":[OSD([sQuery(id+"F2.wireOp",EDGE,"E22")])],"isStart":false});
            var Q1;
            {var subQ0=sQuery(id+"F0.wireOp",EDGE,"E18.2.4");var subQ1=sQuery(id+"F0.wireOp",EDGE,"E18.1.3");var subQ2=sQuery(id+"F0.wireOp",EDGE,"E18.1.4");var subQ3=sQuery(id+"F0.wireOp",EDGE,"E18.2.3");var subQ4=sQuery(id+"F0.wireOp",EDGE,"E18.2.5");var subQ5=sQuery(id+"F0.wireOp",EDGE,"E18.3.18");var subQ6=sQuery(id+"F0.wireOp",EDGE,"E18.3.12");var subQ7=sQuery(id+"F0.wireOp",EDGE,"E18.2.2");var subQ8=sQuery(id+"F0.wireOp",EDGE,"E18.1.1");var subQ9=sQuery(id+"F0.wireOp",EDGE,"E18.2.1");var subQ10=sQuery(id+"F0.wireOp",EDGE,"E18.1.18");var subQ11=sQuery(id+"F0.wireOp",EDGE,"E18.1.12");var subQ12=sQuery(id+"F0.wireOp",EDGE,"E18.1.2");var subQ13=sQuery(id+"F0.wireOp",EDGE,"E18.2.18");var subQ14=sQuery(id+"F0.wireOp",EDGE,"E18.2.12");var subQ15=sQuery(id+"F0.wireOp",EDGE,"E12.MirrorCS");var subQ16=sQuery(id+"F0.wireOp",EDGE,"E5");var subQ17=sQuery(id+"F0.wireOp",EDGE,"E8");var subQ18=sQuery(id+"F0.wireOp",EDGE,"E18.5.18");var subQ19=sQuery(id+"F0.wireOp",EDGE,"E18.5.12");var subQ20=sQuery(id+"F0.wireOp",EDGE,"E7");var subQ21=sQuery(id+"F0.wireOp",EDGE,"E18.1.6");var subQ22=sQuery(id+"F0.wireOp",EDGE,"E11");var subQ23=sQuery(id+"F0.wireOp",EDGE,"E16");var subQ24=sQuery(id+"F0.wireOp",EDGE,"E18.3.6");var subQ25=sQuery(id+"F0.wireOp",EDGE,"E18.2.0");var subQ26=sQuery(id+"F0.wireOp",EDGE,"E13.MirrorCS");var subQ27=sQuery(id+"F0.wireOp",EDGE,"E14.MirrorCS");var subQ28=sQuery(id+"F0.wireOp",EDGE,"E18.1.5");var subQ29=sQuery(id+"F0.wireOp",EDGE,"E18.5.0");var subQ30=sQuery(id+"F0.wireOp",EDGE,"E15.MirrorCS");var subQ31=sQuery(id+"F0.wireOp",EDGE,"E18.2.6");var subQ32=sQuery(id+"F0.wireOp",EDGE,"E18.1.0");var subQ33=sQuery(id+"F0.wireOp",EDGE,"E18.4.6");var subQ34=sQuery(id+"F0.wireOp",EDGE,"E18.3.0");var subQ35=sQuery(id+"F0.wireOp",EDGE,"E18.3.2");var subQ36=sQuery(id+"F0.wireOp",EDGE,"E18.4.1");var subQ37=sQuery(id+"F0.wireOp",EDGE,"E18.4.3");var subQ38=sQuery(id+"F0.wireOp",EDGE,"E18.3.1");var subQ39=sQuery(id+"F0.wireOp",EDGE,"E18.3.3");var subQ40=sQuery(id+"F0.wireOp",EDGE,"E18.3.4");var subQ41=sQuery(id+"F0.wireOp",EDGE,"E18.4.5");var subQ42=sQuery(id+"F0.wireOp",EDGE,"E18.5.1");var subQ43=sQuery(id+"F0.wireOp",EDGE,"E18.3.5");var subQ44=sQuery(id+"F0.wireOp",EDGE,"E18.5.6");var subQ45=sQuery(id+"F0.wireOp",EDGE,"E18.4.0");var subQ46=sQuery(id+"F0.wireOp",EDGE,"E18.4.2");var subQ47=sQuery(id+"F0.wireOp",EDGE,"E18.4.4");var subQ48=sQuery(id+"F0.wireOp",EDGE,"E18.4.18");var subQ49=sQuery(id+"F0.wireOp",EDGE,"E18.4.12");var subQ50=sQuery(id+"F0.wireOp",EDGE,"E18.5.2");var subQ51=sQuery(id+"F0.wireOp",EDGE,"E18.5.4");var subQ52=sQuery(id+"F0.wireOp",EDGE,"E18.5.3");var subQ53=sQuery(id+"F0.wireOp",EDGE,"E18.5.5");Q1=makeQuery(id+"F10.boolean.opBoolean","INTERSECT",EDGE,{"derivedFrom":[makeQuery(id+"F3.boolean.opBoolean","SPLIT",FACE,{"disambiguationData":[TD([makeQuery(id+"F1.opExtrude","SWEPT_FACE",FACE,{"disambiguationData":[OSD([subQ20])]})])],"derivedFrom":makeQuery(id+"F1.opExtrude","CAP_FACE",FACE,{"disambiguationData":[OSD([sQuery(id+"F0.wireOp",EDGE,"E1"),subQ22,subQ20,subQ17,subQ16,subQ15,subQ26,subQ27,subQ30,subQ23,subQ32,subQ8,subQ12,subQ1,subQ2,subQ28,subQ21,subQ11,subQ10,subQ25,subQ9,subQ7,subQ3,subQ0,subQ4,subQ31,subQ14,subQ13,subQ34,subQ38,subQ35,subQ39,subQ40,subQ43,subQ24,subQ6,subQ5,subQ45,subQ36,subQ46,subQ37,subQ47,subQ41,subQ33,subQ49,subQ48,subQ29,subQ42,subQ50,subQ52,subQ51,subQ53,subQ44,subQ19,subQ18,sQuery(id+"F0.wireOp",EDGE,"E19.bottom"),sQuery(id+"F0.wireOp",EDGE,"E19.top"),sQuery(id+"F0.wireOp",EDGE,"E19.left"),sQuery(id+"F0.wireOp",EDGE,"E19.right"),sQuery(id+"F0.wireOp",EDGE,"E20.trimOffspring")])],"isStart":true})}),makeQuery(id+"F10.opExtrude","SWEPT_FACE",FACE,{"disambiguationData":[OSD([sQuery(id+"F9.wireOp",EDGE,"E39.4.5")])]})]});}
            var Q2;
            {var subQ0=sQuery(id+"F0.wireOp",EDGE,"E18.2.4");var subQ1=sQuery(id+"F0.wireOp",EDGE,"E18.1.3");var subQ2=sQuery(id+"F0.wireOp",EDGE,"E18.1.4");var subQ3=sQuery(id+"F0.wireOp",EDGE,"E18.2.3");var subQ4=sQuery(id+"F0.wireOp",EDGE,"E18.2.5");var subQ5=sQuery(id+"F0.wireOp",EDGE,"E18.3.18");var subQ6=sQuery(id+"F0.wireOp",EDGE,"E18.3.12");var subQ7=sQuery(id+"F0.wireOp",EDGE,"E18.2.2");var subQ8=sQuery(id+"F0.wireOp",EDGE,"E18.1.1");var subQ9=sQuery(id+"F0.wireOp",EDGE,"E18.2.1");var subQ10=sQuery(id+"F0.wireOp",EDGE,"E18.1.18");var subQ11=sQuery(id+"F0.wireOp",EDGE,"E18.1.12");var subQ12=sQuery(id+"F0.wireOp",EDGE,"E18.1.2");var subQ13=sQuery(id+"F0.wireOp",EDGE,"E18.2.18");var subQ14=sQuery(id+"F0.wireOp",EDGE,"E18.2.12");var subQ15=sQuery(id+"F0.wireOp",EDGE,"E12.MirrorCS");var subQ16=sQuery(id+"F0.wireOp",EDGE,"E5");var subQ17=sQuery(id+"F0.wireOp",EDGE,"E8");var subQ18=sQuery(id+"F0.wireOp",EDGE,"E18.5.18");var subQ19=sQuery(id+"F0.wireOp",EDGE,"E18.5.12");var subQ20=sQuery(id+"F0.wireOp",EDGE,"E7");var subQ21=sQuery(id+"F0.wireOp",EDGE,"E18.1.6");var subQ22=sQuery(id+"F0.wireOp",EDGE,"E11");var subQ23=sQuery(id+"F0.wireOp",EDGE,"E16");var subQ24=sQuery(id+"F0.wireOp",EDGE,"E18.3.6");var subQ25=sQuery(id+"F0.wireOp",EDGE,"E18.2.0");var subQ26=sQuery(id+"F0.wireOp",EDGE,"E13.MirrorCS");var subQ27=sQuery(id+"F0.wireOp",EDGE,"E14.MirrorCS");var subQ28=sQuery(id+"F0.wireOp",EDGE,"E18.1.5");var subQ29=sQuery(id+"F0.wireOp",EDGE,"E18.5.0");var subQ30=sQuery(id+"F0.wireOp",EDGE,"E15.MirrorCS");var subQ31=sQuery(id+"F0.wireOp",EDGE,"E18.2.6");var subQ32=sQuery(id+"F0.wireOp",EDGE,"E18.1.0");var subQ33=sQuery(id+"F0.wireOp",EDGE,"E18.4.6");var subQ34=sQuery(id+"F0.wireOp",EDGE,"E18.3.0");var subQ35=sQuery(id+"F0.wireOp",EDGE,"E18.3.2");var subQ36=sQuery(id+"F0.wireOp",EDGE,"E18.4.1");var subQ37=sQuery(id+"F0.wireOp",EDGE,"E18.4.3");var subQ38=sQuery(id+"F0.wireOp",EDGE,"E18.3.1");var subQ39=sQuery(id+"F0.wireOp",EDGE,"E18.3.3");var subQ40=sQuery(id+"F0.wireOp",EDGE,"E18.3.4");var subQ41=sQuery(id+"F0.wireOp",EDGE,"E18.4.5");var subQ42=sQuery(id+"F0.wireOp",EDGE,"E18.5.1");var subQ43=sQuery(id+"F0.wireOp",EDGE,"E18.3.5");var subQ44=sQuery(id+"F0.wireOp",EDGE,"E18.5.6");var subQ45=sQuery(id+"F0.wireOp",EDGE,"E18.4.0");var subQ46=sQuery(id+"F0.wireOp",EDGE,"E18.4.2");var subQ47=sQuery(id+"F0.wireOp",EDGE,"E18.4.4");var subQ48=sQuery(id+"F0.wireOp",EDGE,"E18.4.18");var subQ49=sQuery(id+"F0.wireOp",EDGE,"E18.4.12");var subQ50=sQuery(id+"F0.wireOp",EDGE,"E18.5.2");var subQ51=sQuery(id+"F0.wireOp",EDGE,"E18.5.4");var subQ52=sQuery(id+"F0.wireOp",EDGE,"E18.5.3");var subQ53=sQuery(id+"F0.wireOp",EDGE,"E18.5.5");Q2=makeQuery(id+"F10.boolean.opBoolean","INTERSECT",EDGE,{"derivedFrom":[makeQuery(id+"F3.boolean.opBoolean","SPLIT",FACE,{"disambiguationData":[TD([makeQuery(id+"F1.opExtrude","SWEPT_FACE",FACE,{"disambiguationData":[OSD([subQ20])]})])],"derivedFrom":makeQuery(id+"F1.opExtrude","CAP_FACE",FACE,{"disambiguationData":[OSD([sQuery(id+"F0.wireOp",EDGE,"E1"),subQ22,subQ20,subQ17,subQ16,subQ15,subQ26,subQ27,subQ30,subQ23,subQ32,subQ8,subQ12,subQ1,subQ2,subQ28,subQ21,subQ11,subQ10,subQ25,subQ9,subQ7,subQ3,subQ0,subQ4,subQ31,subQ14,subQ13,subQ34,subQ38,subQ35,subQ39,subQ40,subQ43,subQ24,subQ6,subQ5,subQ45,subQ36,subQ46,subQ37,subQ47,subQ41,subQ33,subQ49,subQ48,subQ29,subQ42,subQ50,subQ52,subQ51,subQ53,subQ44,subQ19,subQ18,sQuery(id+"F0.wireOp",EDGE,"E19.bottom"),sQuery(id+"F0.wireOp",EDGE,"E19.top"),sQuery(id+"F0.wireOp",EDGE,"E19.left"),sQuery(id+"F0.wireOp",EDGE,"E19.right"),sQuery(id+"F0.wireOp",EDGE,"E20.trimOffspring")])],"isStart":true})}),makeQuery(id+"F10.opExtrude","SWEPT_FACE",FACE,{"disambiguationData":[OSD([sQuery(id+"F9.wireOp",EDGE,"E39.3.5")])]})]});}
            var Q3;
            {var subQ0=sQuery(id+"F0.wireOp",EDGE,"E18.2.4");var subQ1=sQuery(id+"F0.wireOp",EDGE,"E18.1.3");var subQ2=sQuery(id+"F0.wireOp",EDGE,"E18.1.4");var subQ3=sQuery(id+"F0.wireOp",EDGE,"E18.2.3");var subQ4=sQuery(id+"F0.wireOp",EDGE,"E18.2.5");var subQ5=sQuery(id+"F0.wireOp",EDGE,"E18.3.18");var subQ6=sQuery(id+"F0.wireOp",EDGE,"E18.3.12");var subQ7=sQuery(id+"F0.wireOp",EDGE,"E18.2.2");var subQ8=sQuery(id+"F0.wireOp",EDGE,"E18.1.1");var subQ9=sQuery(id+"F0.wireOp",EDGE,"E18.2.1");var subQ10=sQuery(id+"F0.wireOp",EDGE,"E18.1.18");var subQ11=sQuery(id+"F0.wireOp",EDGE,"E18.1.12");var subQ12=sQuery(id+"F0.wireOp",EDGE,"E18.1.2");var subQ13=sQuery(id+"F0.wireOp",EDGE,"E18.2.18");var subQ14=sQuery(id+"F0.wireOp",EDGE,"E18.2.12");var subQ15=sQuery(id+"F0.wireOp",EDGE,"E12.MirrorCS");var subQ16=sQuery(id+"F0.wireOp",EDGE,"E5");var subQ17=sQuery(id+"F0.wireOp",EDGE,"E8");var subQ18=sQuery(id+"F0.wireOp",EDGE,"E18.5.18");var subQ19=sQuery(id+"F0.wireOp",EDGE,"E18.5.12");var subQ20=sQuery(id+"F0.wireOp",EDGE,"E7");var subQ21=sQuery(id+"F0.wireOp",EDGE,"E18.1.6");var subQ22=sQuery(id+"F0.wireOp",EDGE,"E11");var subQ23=sQuery(id+"F0.wireOp",EDGE,"E16");var subQ24=sQuery(id+"F0.wireOp",EDGE,"E18.3.6");var subQ25=sQuery(id+"F0.wireOp",EDGE,"E18.2.0");var subQ26=sQuery(id+"F0.wireOp",EDGE,"E13.MirrorCS");var subQ27=sQuery(id+"F0.wireOp",EDGE,"E14.MirrorCS");var subQ28=sQuery(id+"F0.wireOp",EDGE,"E18.1.5");var subQ29=sQuery(id+"F0.wireOp",EDGE,"E18.5.0");var subQ30=sQuery(id+"F0.wireOp",EDGE,"E15.MirrorCS");var subQ31=sQuery(id+"F0.wireOp",EDGE,"E18.2.6");var subQ32=sQuery(id+"F0.wireOp",EDGE,"E18.1.0");var subQ33=sQuery(id+"F0.wireOp",EDGE,"E18.4.6");var subQ34=sQuery(id+"F0.wireOp",EDGE,"E18.3.0");var subQ35=sQuery(id+"F0.wireOp",EDGE,"E18.3.2");var subQ36=sQuery(id+"F0.wireOp",EDGE,"E18.4.1");var subQ37=sQuery(id+"F0.wireOp",EDGE,"E18.4.3");var subQ38=sQuery(id+"F0.wireOp",EDGE,"E18.3.1");var subQ39=sQuery(id+"F0.wireOp",EDGE,"E18.3.3");var subQ40=sQuery(id+"F0.wireOp",EDGE,"E18.3.4");var subQ41=sQuery(id+"F0.wireOp",EDGE,"E18.4.5");var subQ42=sQuery(id+"F0.wireOp",EDGE,"E18.5.1");var subQ43=sQuery(id+"F0.wireOp",EDGE,"E18.3.5");var subQ44=sQuery(id+"F0.wireOp",EDGE,"E18.5.6");var subQ45=sQuery(id+"F0.wireOp",EDGE,"E18.4.0");var subQ46=sQuery(id+"F0.wireOp",EDGE,"E18.4.2");var subQ47=sQuery(id+"F0.wireOp",EDGE,"E18.4.4");var subQ48=sQuery(id+"F0.wireOp",EDGE,"E18.4.18");var subQ49=sQuery(id+"F0.wireOp",EDGE,"E18.4.12");var subQ50=sQuery(id+"F0.wireOp",EDGE,"E18.5.2");var subQ51=sQuery(id+"F0.wireOp",EDGE,"E18.5.4");var subQ52=sQuery(id+"F0.wireOp",EDGE,"E18.5.3");var subQ53=sQuery(id+"F0.wireOp",EDGE,"E18.5.5");Q3=makeQuery(id+"F10.boolean.opBoolean","INTERSECT",EDGE,{"derivedFrom":[makeQuery(id+"F3.boolean.opBoolean","SPLIT",FACE,{"disambiguationData":[TD([makeQuery(id+"F1.opExtrude","SWEPT_FACE",FACE,{"disambiguationData":[OSD([subQ20])]})])],"derivedFrom":makeQuery(id+"F1.opExtrude","CAP_FACE",FACE,{"disambiguationData":[OSD([sQuery(id+"F0.wireOp",EDGE,"E1"),subQ22,subQ20,subQ17,subQ16,subQ15,subQ26,subQ27,subQ30,subQ23,subQ32,subQ8,subQ12,subQ1,subQ2,subQ28,subQ21,subQ11,subQ10,subQ25,subQ9,subQ7,subQ3,subQ0,subQ4,subQ31,subQ14,subQ13,subQ34,subQ38,subQ35,subQ39,subQ40,subQ43,subQ24,subQ6,subQ5,subQ45,subQ36,subQ46,subQ37,subQ47,subQ41,subQ33,subQ49,subQ48,subQ29,subQ42,subQ50,subQ52,subQ51,subQ53,subQ44,subQ19,subQ18,sQuery(id+"F0.wireOp",EDGE,"E19.bottom"),sQuery(id+"F0.wireOp",EDGE,"E19.top"),sQuery(id+"F0.wireOp",EDGE,"E19.left"),sQuery(id+"F0.wireOp",EDGE,"E19.right"),sQuery(id+"F0.wireOp",EDGE,"E20.trimOffspring")])],"isStart":true})}),makeQuery(id+"F10.opExtrude","SWEPT_FACE",FACE,{"disambiguationData":[OSD([sQuery(id+"F9.wireOp",EDGE,"E39.2.5")])]})]});}
            var Q4;
            {var subQ0=sQuery(id+"F0.wireOp",EDGE,"E18.2.4");var subQ1=sQuery(id+"F0.wireOp",EDGE,"E18.1.3");var subQ2=sQuery(id+"F0.wireOp",EDGE,"E18.1.4");var subQ3=sQuery(id+"F0.wireOp",EDGE,"E18.2.3");var subQ4=sQuery(id+"F0.wireOp",EDGE,"E18.2.5");var subQ5=sQuery(id+"F0.wireOp",EDGE,"E18.3.18");var subQ6=sQuery(id+"F0.wireOp",EDGE,"E18.3.12");var subQ7=sQuery(id+"F0.wireOp",EDGE,"E18.2.2");var subQ8=sQuery(id+"F0.wireOp",EDGE,"E18.1.1");var subQ9=sQuery(id+"F0.wireOp",EDGE,"E18.2.1");var subQ10=sQuery(id+"F0.wireOp",EDGE,"E18.1.18");var subQ11=sQuery(id+"F0.wireOp",EDGE,"E18.1.12");var subQ12=sQuery(id+"F0.wireOp",EDGE,"E18.1.2");var subQ13=sQuery(id+"F0.wireOp",EDGE,"E18.2.18");var subQ14=sQuery(id+"F0.wireOp",EDGE,"E18.2.12");var subQ15=sQuery(id+"F0.wireOp",EDGE,"E12.MirrorCS");var subQ16=sQuery(id+"F0.wireOp",EDGE,"E5");var subQ17=sQuery(id+"F0.wireOp",EDGE,"E8");var subQ18=sQuery(id+"F0.wireOp",EDGE,"E18.5.18");var subQ19=sQuery(id+"F0.wireOp",EDGE,"E18.5.12");var subQ20=sQuery(id+"F0.wireOp",EDGE,"E7");var subQ21=sQuery(id+"F0.wireOp",EDGE,"E18.1.6");var subQ22=sQuery(id+"F0.wireOp",EDGE,"E11");var subQ23=sQuery(id+"F0.wireOp",EDGE,"E16");var subQ24=sQuery(id+"F0.wireOp",EDGE,"E18.3.6");var subQ25=sQuery(id+"F0.wireOp",EDGE,"E18.2.0");var subQ26=sQuery(id+"F0.wireOp",EDGE,"E13.MirrorCS");var subQ27=sQuery(id+"F0.wireOp",EDGE,"E14.MirrorCS");var subQ28=sQuery(id+"F0.wireOp",EDGE,"E18.1.5");var subQ29=sQuery(id+"F0.wireOp",EDGE,"E18.5.0");var subQ30=sQuery(id+"F0.wireOp",EDGE,"E15.MirrorCS");var subQ31=sQuery(id+"F0.wireOp",EDGE,"E18.2.6");var subQ32=sQuery(id+"F0.wireOp",EDGE,"E18.1.0");var subQ33=sQuery(id+"F0.wireOp",EDGE,"E18.4.6");var subQ34=sQuery(id+"F0.wireOp",EDGE,"E18.3.0");var subQ35=sQuery(id+"F0.wireOp",EDGE,"E18.3.2");var subQ36=sQuery(id+"F0.wireOp",EDGE,"E18.4.1");var subQ37=sQuery(id+"F0.wireOp",EDGE,"E18.4.3");var subQ38=sQuery(id+"F0.wireOp",EDGE,"E18.3.1");var subQ39=sQuery(id+"F0.wireOp",EDGE,"E18.3.3");var subQ40=sQuery(id+"F0.wireOp",EDGE,"E18.3.4");var subQ41=sQuery(id+"F0.wireOp",EDGE,"E18.4.5");var subQ42=sQuery(id+"F0.wireOp",EDGE,"E18.5.1");var subQ43=sQuery(id+"F0.wireOp",EDGE,"E18.3.5");var subQ44=sQuery(id+"F0.wireOp",EDGE,"E18.5.6");var subQ45=sQuery(id+"F0.wireOp",EDGE,"E18.4.0");var subQ46=sQuery(id+"F0.wireOp",EDGE,"E18.4.2");var subQ47=sQuery(id+"F0.wireOp",EDGE,"E18.4.4");var subQ48=sQuery(id+"F0.wireOp",EDGE,"E18.4.18");var subQ49=sQuery(id+"F0.wireOp",EDGE,"E18.4.12");var subQ50=sQuery(id+"F0.wireOp",EDGE,"E18.5.2");var subQ51=sQuery(id+"F0.wireOp",EDGE,"E18.5.4");var subQ52=sQuery(id+"F0.wireOp",EDGE,"E18.5.3");var subQ53=sQuery(id+"F0.wireOp",EDGE,"E18.5.5");Q4=makeQuery(id+"F10.boolean.opBoolean","INTERSECT",EDGE,{"derivedFrom":[makeQuery(id+"F3.boolean.opBoolean","SPLIT",FACE,{"disambiguationData":[TD([makeQuery(id+"F1.opExtrude","SWEPT_FACE",FACE,{"disambiguationData":[OSD([subQ20])]})])],"derivedFrom":makeQuery(id+"F1.opExtrude","CAP_FACE",FACE,{"disambiguationData":[OSD([sQuery(id+"F0.wireOp",EDGE,"E1"),subQ22,subQ20,subQ17,subQ16,subQ15,subQ26,subQ27,subQ30,subQ23,subQ32,subQ8,subQ12,subQ1,subQ2,subQ28,subQ21,subQ11,subQ10,subQ25,subQ9,subQ7,subQ3,subQ0,subQ4,subQ31,subQ14,subQ13,subQ34,subQ38,subQ35,subQ39,subQ40,subQ43,subQ24,subQ6,subQ5,subQ45,subQ36,subQ46,subQ37,subQ47,subQ41,subQ33,subQ49,subQ48,subQ29,subQ42,subQ50,subQ52,subQ51,subQ53,subQ44,subQ19,subQ18,sQuery(id+"F0.wireOp",EDGE,"E19.bottom"),sQuery(id+"F0.wireOp",EDGE,"E19.top"),sQuery(id+"F0.wireOp",EDGE,"E19.left"),sQuery(id+"F0.wireOp",EDGE,"E19.right"),sQuery(id+"F0.wireOp",EDGE,"E20.trimOffspring")])],"isStart":true})}),makeQuery(id+"F10.opExtrude","SWEPT_FACE",FACE,{"disambiguationData":[OSD([sQuery(id+"F9.wireOp",EDGE,"E36.right")])]})]});}
            var Q5;
            {var subQ0=sQuery(id+"F0.wireOp",EDGE,"E18.2.4");var subQ1=sQuery(id+"F0.wireOp",EDGE,"E18.1.3");var subQ2=sQuery(id+"F0.wireOp",EDGE,"E18.1.4");var subQ3=sQuery(id+"F0.wireOp",EDGE,"E18.2.3");var subQ4=sQuery(id+"F0.wireOp",EDGE,"E18.2.5");var subQ5=sQuery(id+"F0.wireOp",EDGE,"E18.3.18");var subQ6=sQuery(id+"F0.wireOp",EDGE,"E18.3.12");var subQ7=sQuery(id+"F0.wireOp",EDGE,"E18.2.2");var subQ8=sQuery(id+"F0.wireOp",EDGE,"E18.1.1");var subQ9=sQuery(id+"F0.wireOp",EDGE,"E18.2.1");var subQ10=sQuery(id+"F0.wireOp",EDGE,"E18.1.18");var subQ11=sQuery(id+"F0.wireOp",EDGE,"E18.1.12");var subQ12=sQuery(id+"F0.wireOp",EDGE,"E18.1.2");var subQ13=sQuery(id+"F0.wireOp",EDGE,"E18.2.18");var subQ14=sQuery(id+"F0.wireOp",EDGE,"E18.2.12");var subQ15=sQuery(id+"F0.wireOp",EDGE,"E12.MirrorCS");var subQ16=sQuery(id+"F0.wireOp",EDGE,"E5");var subQ17=sQuery(id+"F0.wireOp",EDGE,"E8");var subQ18=sQuery(id+"F0.wireOp",EDGE,"E18.5.18");var subQ19=sQuery(id+"F0.wireOp",EDGE,"E18.5.12");var subQ20=sQuery(id+"F0.wireOp",EDGE,"E7");var subQ21=sQuery(id+"F0.wireOp",EDGE,"E18.1.6");var subQ22=sQuery(id+"F0.wireOp",EDGE,"E11");var subQ23=sQuery(id+"F0.wireOp",EDGE,"E16");var subQ24=sQuery(id+"F0.wireOp",EDGE,"E18.3.6");var subQ25=sQuery(id+"F0.wireOp",EDGE,"E18.2.0");var subQ26=sQuery(id+"F0.wireOp",EDGE,"E13.MirrorCS");var subQ27=sQuery(id+"F0.wireOp",EDGE,"E14.MirrorCS");var subQ28=sQuery(id+"F0.wireOp",EDGE,"E18.1.5");var subQ29=sQuery(id+"F0.wireOp",EDGE,"E18.5.0");var subQ30=sQuery(id+"F0.wireOp",EDGE,"E15.MirrorCS");var subQ31=sQuery(id+"F0.wireOp",EDGE,"E18.2.6");var subQ32=sQuery(id+"F0.wireOp",EDGE,"E18.1.0");var subQ33=sQuery(id+"F0.wireOp",EDGE,"E18.4.6");var subQ34=sQuery(id+"F0.wireOp",EDGE,"E18.3.0");var subQ35=sQuery(id+"F0.wireOp",EDGE,"E18.3.2");var subQ36=sQuery(id+"F0.wireOp",EDGE,"E18.4.1");var subQ37=sQuery(id+"F0.wireOp",EDGE,"E18.4.3");var subQ38=sQuery(id+"F0.wireOp",EDGE,"E18.3.1");var subQ39=sQuery(id+"F0.wireOp",EDGE,"E18.3.3");var subQ40=sQuery(id+"F0.wireOp",EDGE,"E18.3.4");var subQ41=sQuery(id+"F0.wireOp",EDGE,"E18.4.5");var subQ42=sQuery(id+"F0.wireOp",EDGE,"E18.5.1");var subQ43=sQuery(id+"F0.wireOp",EDGE,"E18.3.5");var subQ44=sQuery(id+"F0.wireOp",EDGE,"E18.5.6");var subQ45=sQuery(id+"F0.wireOp",EDGE,"E18.4.0");var subQ46=sQuery(id+"F0.wireOp",EDGE,"E18.4.2");var subQ47=sQuery(id+"F0.wireOp",EDGE,"E18.4.4");var subQ48=sQuery(id+"F0.wireOp",EDGE,"E18.4.18");var subQ49=sQuery(id+"F0.wireOp",EDGE,"E18.4.12");var subQ50=sQuery(id+"F0.wireOp",EDGE,"E18.5.2");var subQ51=sQuery(id+"F0.wireOp",EDGE,"E18.5.4");var subQ52=sQuery(id+"F0.wireOp",EDGE,"E18.5.3");var subQ53=sQuery(id+"F0.wireOp",EDGE,"E18.5.5");Q5=makeQuery(id+"F10.boolean.opBoolean","INTERSECT",EDGE,{"derivedFrom":[makeQuery(id+"F3.boolean.opBoolean","SPLIT",FACE,{"disambiguationData":[TD([makeQuery(id+"F1.opExtrude","SWEPT_FACE",FACE,{"disambiguationData":[OSD([subQ20])]})])],"derivedFrom":makeQuery(id+"F1.opExtrude","CAP_FACE",FACE,{"disambiguationData":[OSD([sQuery(id+"F0.wireOp",EDGE,"E1"),subQ22,subQ20,subQ17,subQ16,subQ15,subQ26,subQ27,subQ30,subQ23,subQ32,subQ8,subQ12,subQ1,subQ2,subQ28,subQ21,subQ11,subQ10,subQ25,subQ9,subQ7,subQ3,subQ0,subQ4,subQ31,subQ14,subQ13,subQ34,subQ38,subQ35,subQ39,subQ40,subQ43,subQ24,subQ6,subQ5,subQ45,subQ36,subQ46,subQ37,subQ47,subQ41,subQ33,subQ49,subQ48,subQ29,subQ42,subQ50,subQ52,subQ51,subQ53,subQ44,subQ19,subQ18,sQuery(id+"F0.wireOp",EDGE,"E19.bottom"),sQuery(id+"F0.wireOp",EDGE,"E19.top"),sQuery(id+"F0.wireOp",EDGE,"E19.left"),sQuery(id+"F0.wireOp",EDGE,"E19.right"),sQuery(id+"F0.wireOp",EDGE,"E20.trimOffspring")])],"isStart":true})}),makeQuery(id+"F10.opExtrude","SWEPT_FACE",FACE,{"disambiguationData":[OSD([sQuery(id+"F9.wireOp",EDGE,"E39.5.5")])]})]});}
            var Q6;
            Q6=makeQuery(id+"F1.opExtrude","CAP_EDGE",EDGE,{"disambiguationData":[OSD([sQuery(id+"F0.wireOp",EDGE,"E18.5.3")])],"isStart":true});
            var Q7;
            Q7=makeQuery(id+"F1.opExtrude","CAP_EDGE",EDGE,{"disambiguationData":[OSD([sQuery(id+"F0.wireOp",EDGE,"E18.4.3")])],"isStart":true});
            var Q8;
            Q8=makeQuery(id+"F1.opExtrude","CAP_EDGE",EDGE,{"disambiguationData":[OSD([sQuery(id+"F0.wireOp",EDGE,"E18.3.3")])],"isStart":true});
            var Q9;
            Q9=makeQuery(id+"F1.opExtrude","SWEPT_FACE",FACE,{"disambiguationData":[OSD([sQuery(id+"F0.wireOp",EDGE,"E18.2.3")])]});
            var Q10;
            Q10=makeQuery(id+"F1.opExtrude","CAP_EDGE",EDGE,{"disambiguationData":[OSD([sQuery(id+"F0.wireOp",EDGE,"E18.1.3")])],"isStart":true});
            var Q11;
            Q11=makeQuery(id+"F1.opExtrude","CAP_EDGE",EDGE,{"disambiguationData":[OSD([sQuery(id+"F0.wireOp",EDGE,"E16")])],"isStart":true});
            var Q12;
            Q12=makeQuery(id+"F1.opExtrude","CAP_EDGE",EDGE,{"disambiguationData":[OSD([sQuery(id+"F0.wireOp",EDGE,"E7")])],"isStart":true});
            fillet(context, id + "F14", {"entities" : qUnion([Q0, Q1, Q2, Q3, Q4, Q5, Q6, Q7, Q8, Q9, Q10, Q11, Q12]), "radius" : 0.76 * mm, "tangentPropagation" : true, "allowEdgeOverflow" : false});
        }
    });
